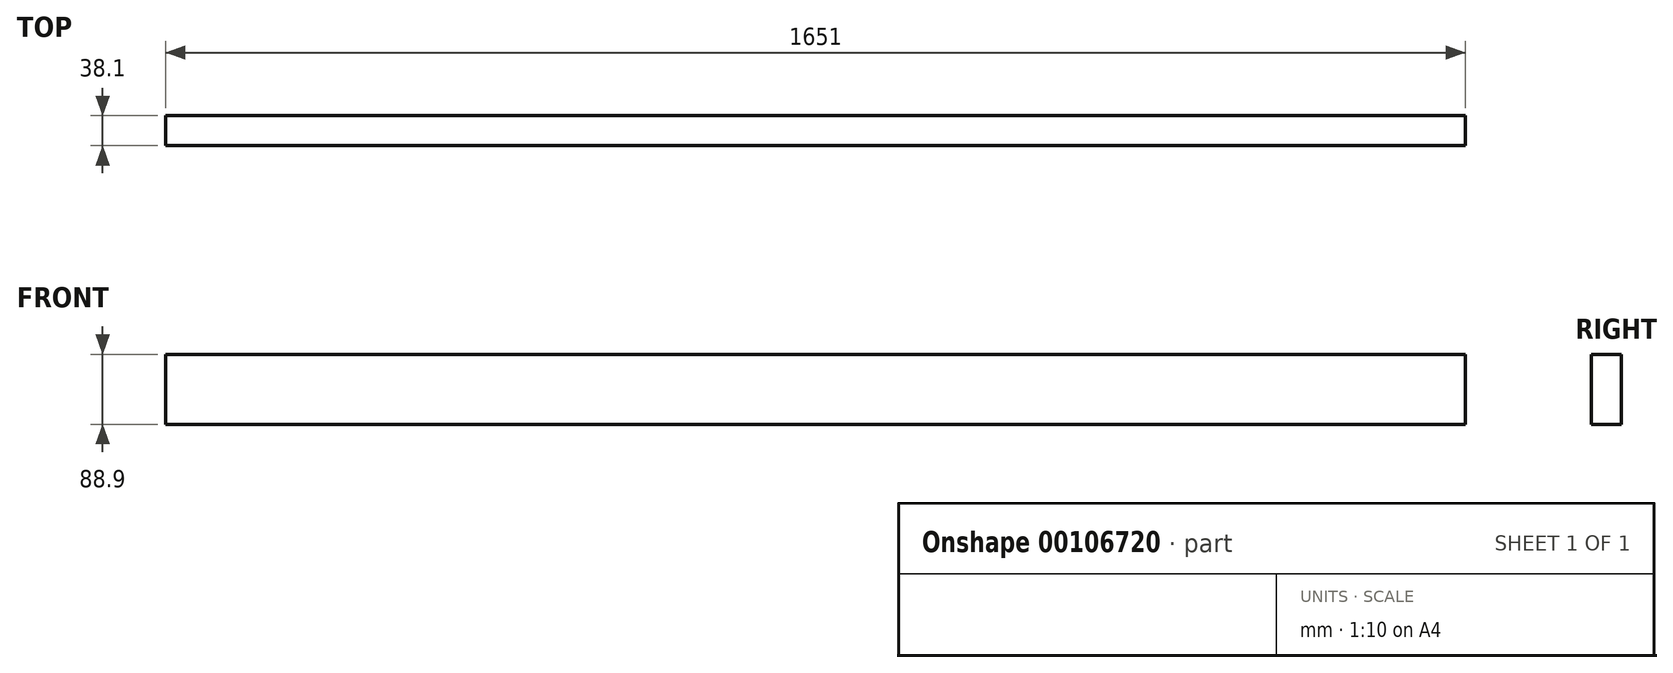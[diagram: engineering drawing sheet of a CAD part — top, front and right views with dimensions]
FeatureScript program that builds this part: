
annotation { "Feature Type Name" : "Feature", "Feature Type Description" : "" }
export const myFeature = defineFeature(function(context is Context, id is Id, definition is map)
    precondition{}
    {
        {
            var Q0;
            Q0=qCreatedBy(makeId("Front.planeOp"),FACE);
            var sketch = newSketch(context, id + "F0", { "sketchPlane" : qUnion([Q0])});
            skLineSegment(sketch, "E0.bottom", {"start": v(0, 0) * mm, "end": v(1651, 0) * mm});
            skLineSegment(sketch, "E0.top", {"start": v(0, 88.9) * mm, "end": v(1651, 88.9) * mm});
            skLineSegment(sketch, "E0.left", {"start": v(0, 0) * mm, "end": v(0, 88.9) * mm});
            skLineSegment(sketch, "E0.right", {"start": v(1651, 0) * mm, "end": v(1651, 88.9) * mm});
            skSolve(sketch);
        }
        {
            var Q0;
            Q0=makeQuery(id+"F0.imprint","IMPRINT",FACE,{"disambiguationData":[TD([[makeQuery(id+"F0.imprint","IMPRINT",EDGE,{"derivedFrom":sQuery(id+"F0.wireOp",EDGE,"E0.bottom")}),1.0]])]});
            extrude(context, id + "F1", {"entities" : qUnion([Q0]), "depth" : 38.1 * mm});
        }
    });
